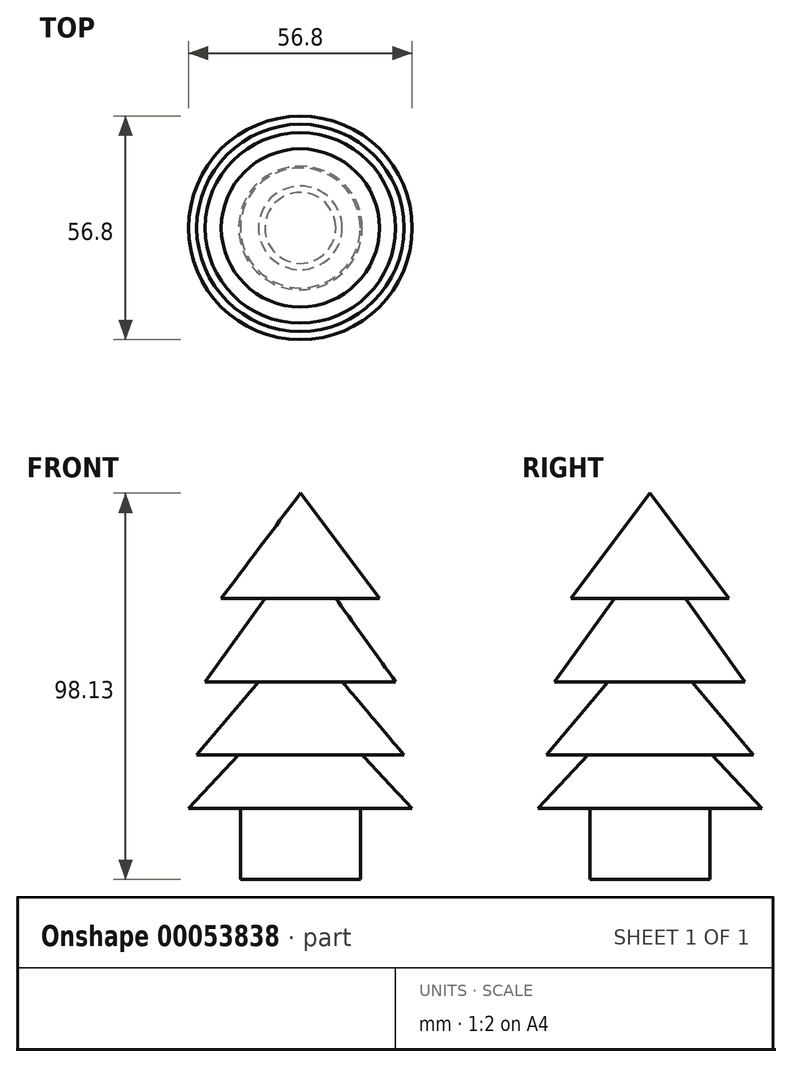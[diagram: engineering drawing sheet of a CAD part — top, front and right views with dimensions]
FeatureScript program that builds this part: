
annotation { "Feature Type Name" : "Feature", "Feature Type Description" : "" }
export const myFeature = defineFeature(function(context is Context, id is Id, definition is map)
    precondition{}
    {
        {
            var Q0;
            Q0=qCreatedBy(makeId("Right.planeOp"),FACE);
            var sketch = newSketch(context, id + "F0", { "sketchPlane" : qUnion([Q0])});
            skLineSegment(sketch, "E0", {"start": v(-17.55, -35.21) * mm, "end": v(-17.55, -53.22) * mm});
            skLineSegment(sketch, "E1", {"start": v(-17.55, -53.22) * mm, "end": v(10.62, -53.22) * mm});
            skLineSegment(sketch, "E2", {"start": v(10.16, -53) * mm, "end": v(10.16, -36.83) * mm});
            skLineSegment(sketch, "E3", {"start": v(10.16, -36.83) * mm, "end": v(28.86, -36.83) * mm});
            skLineSegment(sketch, "E4", {"start": v(28.86, -36.83) * mm, "end": v(18.7, -20.9) * mm});
            skLineSegment(sketch, "E5", {"start": v(18.7, -20.9) * mm, "end": v(28.4, -20.9) * mm});
            skLineSegment(sketch, "E6", {"start": v(28.4, -20.9) * mm, "end": v(12.7, 0) * mm});
            skLineSegment(sketch, "E7", {"start": v(12.7, 0) * mm, "end": v(21.47, 0) * mm});
            skLineSegment(sketch, "E8", {"start": v(21.47, 0) * mm, "end": v(8.08, 19.51) * mm});
            skLineSegment(sketch, "E9", {"start": v(8.08, 19.51) * mm, "end": v(17.55, 19.51) * mm});
            skLineSegment(sketch, "E10", {"start": v(17.55, 19.51) * mm, "end": v(-2.3, 44.91) * mm});
            skLineSegment(sketch, "E11", {"start": v(-17.55, -35.21) * mm, "end": v(-30.71, -35.21) * mm});
            skLineSegment(sketch, "E12", {"start": v(-30.71, -35.21) * mm, "end": v(-18.01, -21.6) * mm});
            skLineSegment(sketch, "E13", {"start": v(-18.01, -21.6) * mm, "end": v(-28.63, -21.6) * mm});
            skLineSegment(sketch, "E14", {"start": v(-28.63, -21.6) * mm, "end": v(-12.93, -2.99) * mm});
            skLineSegment(sketch, "E15", {"start": v(-12.93, -2.99) * mm, "end": v(-26.5, -2.99) * mm});
            skLineSegment(sketch, "E16", {"start": v(-26.5, -2.99) * mm, "end": v(-11.31, 18.13) * mm});
            skLineSegment(sketch, "E17", {"start": v(-11.31, 18.13) * mm, "end": v(-22.4, 18.13) * mm});
            skLineSegment(sketch, "E18", {"start": v(-22.4, 18.13) * mm, "end": v(-2.3, 44.91) * mm});
            skLineSegment(sketch, "E19", {"start": v(-2.3, 44.91) * mm, "end": v(-2.3, -53.22) * mm});
            skSolve(sketch);
        }
        {
            var Q0;
            {var subQ0=sQuery(id+"F0.wireOp",EDGE,"E0");Q0=makeQuery(id+"F0.imprint","IMPRINT",FACE,{"disambiguationData":[TD([[makeQuery(id+"F0.imprint","IMPRINT",EDGE,{"derivedFrom":subQ0}),1.0]])]});}
            var Q1;
            Q1=sQuery(id+"F0.wireOp",EDGE,"E19");
            revolve(context, id + "F1", {"entities" : qUnion([Q0]), "axis" : qUnion([Q1]), "revolveType" : RevolveType.FULL});
        }
    });
